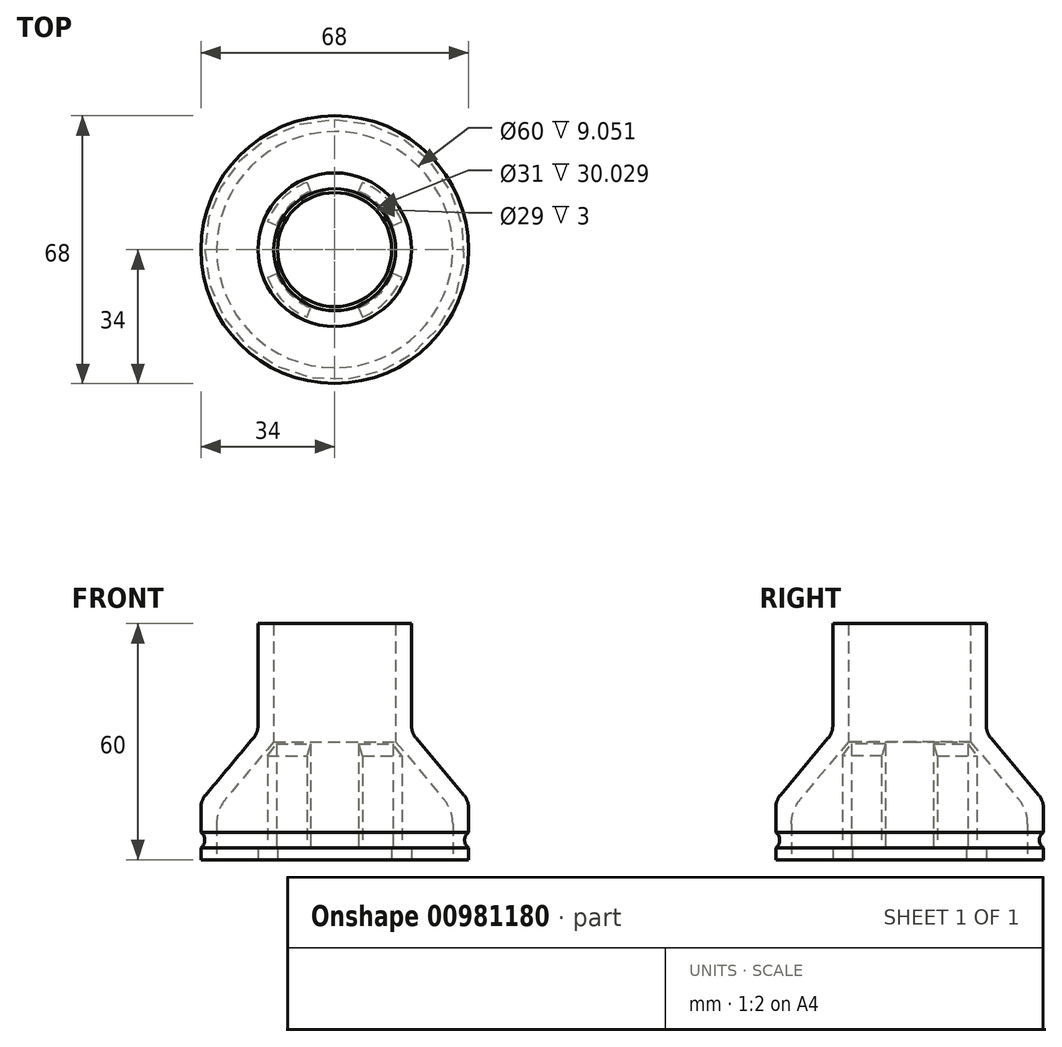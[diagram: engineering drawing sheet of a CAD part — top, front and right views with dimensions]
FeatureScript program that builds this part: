
annotation { "Feature Type Name" : "Feature", "Feature Type Description" : "" }
export const myFeature = defineFeature(function(context is Context, id is Id, definition is map)
    precondition{}
    {
        {
            var Q0;
            Q0=qCreatedBy(makeId("Front.planeOp"),FACE);
            var sketch = newSketch(context, id + "F0", { "sketchPlane" : qUnion([Q0])});
            skLineSegment(sketch, "E0", {"start": v(0, 0) * mm, "end": v(0, 69.55) * mm, "construction": true});
            skLineSegment(sketch, "E1", {"start": v(-30, 0) * mm, "end": v(-30, 12.7) * mm});
            skLineSegment(sketch, "E2", {"start": v(-30, 12.7) * mm, "end": v(-15.5, 29.97) * mm});
            skLineSegment(sketch, "E3", {"start": v(-15.5, 29.97) * mm, "end": v(-15.5, 60) * mm});
            skLineSegment(sketch, "E4", {"start": v(-15.5, 60) * mm, "end": v(-19.5, 60) * mm});
            skLineSegment(sketch, "E5", {"start": v(-19.5, 60) * mm, "end": v(-19.5, 32.28) * mm});
            skLineSegment(sketch, "E6", {"start": v(-19.5, 32.28) * mm, "end": v(-34, 15) * mm});
            skLineSegment(sketch, "E7", {"start": v(-34, 15) * mm, "end": v(-34, 0) * mm});
            skLineSegment(sketch, "E8", {"start": v(-30, 0) * mm, "end": v(-34, 0) * mm});
            skLineSegment(sketch, "E9", {"start": v(-15.5, 29.97) * mm, "end": v(-19.5, 32.28) * mm});
            skLineSegment(sketch, "E10", {"start": v(-30, 12.7) * mm, "end": v(-34, 15) * mm});
            skSolve(sketch);
        }
        {
            var Q0;
            Q0 = qSketchRegion(id + "F0", true);
            var Q1;
            Q1=sQuery(id+"F0.wireOp",EDGE,"E0");
            revolve(context, id + "F1", {"surfaceOperationType" : NewSurfaceOperationType.NEW, "entities" : qUnion([Q0]), "axis" : qUnion([Q1]), "revolveType" : RevolveType.FULL});
        }
        {
            var Q0;
            Q0=makeQuery(id+"F1.opRevolve","SWEPT_FACE",FACE,{"disambiguationData":[OSD([sQuery(id+"F0.wireOp",EDGE,"E8")])]});
            var sketch = newSketch(context, id + "F2", { "sketchPlane" : qUnion([Q0])});
            skCircle(sketch, "E11", {"center": v(0, 0) * mm, "radius": 18.5 * mm});
            skCircle(sketch, "E12", {"center": v(0, 0) * mm, "radius": 16 * mm});
            skLineSegment(sketch, "E13", {"start": v(0, 18.5) * mm, "end": v(0, -18.5) * mm});
            skLineSegment(sketch, "E14", {"start": v(18.5, 0) * mm, "end": v(-18.5, 0) * mm});
            skLineSegment(sketch, "E15", {"start": v(-17.1, -7.08) * mm, "end": v(17.1, 7.08) * mm});
            skLineSegment(sketch, "E16", {"start": v(7.08, 17.1) * mm, "end": v(-7.08, -17.1) * mm});
            skLineSegment(sketch, "E17", {"start": v(17.1, -7.08) * mm, "end": v(-17.1, 7.08) * mm});
            skLineSegment(sketch, "E18", {"start": v(7.08, -17.1) * mm, "end": v(-7.08, 17.1) * mm});
            skSolve(sketch);
        }
        {
            var Q0;
            {var subQ0=sQuery(id+"F2.wireOp",EDGE,"E15");var subQ1=sQuery(id+"F2.wireOp",EDGE,"E11");var subQ2=makeQuery(id+"F2.imprint","INTERSECT",VERTEX,{"disambiguationData":[OD(1.0)],"derivedFrom":[subQ1,subQ0]});Q0=makeQuery(id+"F2.imprint","IMPRINT",FACE,{"disambiguationData":[TD([[makeQuery(id+"F2.imprint","IMPRINT",EDGE,{"disambiguationData":[TD([[subQ2,-1.0]])],"derivedFrom":subQ1}),1.0]])]});}
            var Q1;
            {var subQ0=sQuery(id+"F2.wireOp",EDGE,"E17");var subQ1=sQuery(id+"F2.wireOp",EDGE,"E11");var subQ2=makeQuery(id+"F2.imprint","INTERSECT",VERTEX,{"disambiguationData":[OD(1.0)],"derivedFrom":[subQ1,subQ0]});Q1=makeQuery(id+"F2.imprint","IMPRINT",FACE,{"disambiguationData":[TD([[makeQuery(id+"F2.imprint","IMPRINT",EDGE,{"disambiguationData":[TD([[subQ2,1.0]])],"derivedFrom":subQ1}),1.0]])]});}
            var Q2;
            {var subQ0=sQuery(id+"F2.wireOp",EDGE,"E17");var subQ1=sQuery(id+"F2.wireOp",EDGE,"E11");var subQ2=makeQuery(id+"F2.imprint","INTERSECT",VERTEX,{"disambiguationData":[OD(0.0)],"derivedFrom":[subQ1,subQ0]});Q2=makeQuery(id+"F2.imprint","IMPRINT",FACE,{"disambiguationData":[TD([[makeQuery(id+"F2.imprint","IMPRINT",EDGE,{"disambiguationData":[TD([[subQ2,1.0]])],"derivedFrom":subQ1}),1.0]])]});}
            var Q3;
            {var subQ0=sQuery(id+"F2.wireOp",EDGE,"E15");var subQ1=sQuery(id+"F2.wireOp",EDGE,"E11");var subQ2=makeQuery(id+"F2.imprint","INTERSECT",VERTEX,{"disambiguationData":[OD(0.0)],"derivedFrom":[subQ1,subQ0]});Q3=makeQuery(id+"F2.imprint","IMPRINT",FACE,{"disambiguationData":[TD([[makeQuery(id+"F2.imprint","IMPRINT",EDGE,{"disambiguationData":[TD([[subQ2,-1.0]])],"derivedFrom":subQ1}),1.0]])]});}
            extrude(context, id + "F3", {"entities" : qUnion([Q0, Q1, Q2, Q3]), "operationType" : NewBodyOperationType.ADD, "endBound" : BoundingType.UP_TO_NEXT, "oppositeDirection" : true, "depth" : 25 * mm, "offsetDistance" : 25 * mm});
        }
        {
            var Q0;
            {var subQ0=sQuery(id+"F2.wireOp",EDGE,"E18");var subQ1=sQuery(id+"F2.wireOp",EDGE,"E11");var subQ2=makeQuery(id+"F2.imprint","INTERSECT",VERTEX,{"disambiguationData":[OD(0.0)],"derivedFrom":[subQ1,subQ0]});var subQ3=sQuery(id+"F2.wireOp",EDGE,"E12");var subQ4=makeQuery(id+"F2.imprint","INTERSECT",VERTEX,{"disambiguationData":[OD(1.0)],"derivedFrom":[subQ3,subQ0]});var subQ5=sQuery(id+"F2.wireOp",EDGE,"E17");var subQ6=makeQuery(id+"F2.imprint","INTERSECT",VERTEX,{"disambiguationData":[OD(0.0)],"derivedFrom":[subQ1,subQ5]});Q0=makeQuery(id+"F3.opExtrude","CAP_FACE",FACE,{"disambiguationData":[OSD([subQ1,subQ3,subQ5,subQ0]),TDD([makeQuery(id+"F2.imprint","IMPRINT",EDGE,{"disambiguationData":[TD([[subQ6,1.0]])],"derivedFrom":subQ1}),makeQuery(id+"F2.imprint","IMPRINT",EDGE,{"disambiguationData":[TD([[subQ4,-1.0]])],"derivedFrom":subQ3}),makeQuery(id+"F2.imprint","IMPRINT",EDGE,{"disambiguationData":[TD([[subQ6,-1.0]])],"derivedFrom":subQ5}),makeQuery(id+"F2.imprint","IMPRINT",EDGE,{"disambiguationData":[TD([[subQ2,-1.0]])],"derivedFrom":subQ0})])],"isStart":true});}
            var sketch = newSketch(context, id + "F4", { "sketchPlane" : qUnion([Q0])});
            skCircle(sketch, "E19", {"center": v(0, 0) * mm, "radius": 14.5 * mm});
            skCircle(sketch, "E20", {"center": v(0, 0) * mm, "radius": 19.5 * mm});
            skSolve(sketch);
        }
        {
            var Q0;
            Q0 = qSketchRegion(id + "F4", true);
            extrude(context, id + "F5", {"entities" : qUnion([Q0]), "operationType" : NewBodyOperationType.ADD, "oppositeDirection" : true, "depth" : 3 * mm, "offsetDistance" : 25 * mm});
        }
        {
            var Q0;
            Q0=qCreatedBy(makeId("Front.planeOp"),FACE);
            var sketch = newSketch(context, id + "F6", { "sketchPlane" : qUnion([Q0])});
            skCircle(sketch, "E21", {"center": v(35.5, 5) * mm, "radius": 2.5 * mm});
            skLineSegment(sketch, "E22", {"start": v(0, -8.3) * mm, "end": v(0, 11.78) * mm, "construction": true});
            skSolve(sketch);
        }
        {
            var Q0;
            Q0 = qSketchRegion(id + "F6", true);
            var Q1;
            Q1=sQuery(id+"F6.wireOp",EDGE,"E22");
            revolve(context, id + "F7", {"operationType" : NewBodyOperationType.REMOVE, "surfaceOperationType" : NewSurfaceOperationType.NEW, "entities" : qUnion([Q0]), "axis" : qUnion([Q1]), "revolveType" : RevolveType.FULL, "oppositeDirection" : true});
        }
        {
            var Q0;
            Q0=makeQuery(id+"F1.opRevolve","SWEPT_EDGE",EDGE,{"disambiguationData":[OSD([sQuery(id+"F0.wireOp",EDGE,"E1"),sQuery(id+"F0.wireOp",EDGE,"E2"),sQuery(id+"F0.wireOp",EDGE,"E10")])]});
            fillet(context, id + "F8", {"entities" : qUnion([Q0]), "radius" : 10 * mm, "tangentPropagation" : true, "allowEdgeOverflow" : false});
        }
        {
            var Q0;
            Q0=makeQuery(id+"F1.opRevolve","SWEPT_EDGE",EDGE,{"disambiguationData":[OSD([sQuery(id+"F0.wireOp",EDGE,"E6"),sQuery(id+"F0.wireOp",EDGE,"E7"),sQuery(id+"F0.wireOp",EDGE,"E10")])]});
            fillet(context, id + "F9", {"entities" : qUnion([Q0]), "radius" : 5 * mm, "tangentPropagation" : true, "allowEdgeOverflow" : false});
        }
        {
            var Q0;
            Q0=makeQuery(id+"F1.opRevolve","SWEPT_EDGE",EDGE,{"disambiguationData":[OSD([sQuery(id+"F0.wireOp",EDGE,"E5"),sQuery(id+"F0.wireOp",EDGE,"E6"),sQuery(id+"F0.wireOp",EDGE,"E9")])]});
            fillet(context, id + "F10", {"entities" : qUnion([Q0]), "radius" : 5 * mm, "tangentPropagation" : true, "allowEdgeOverflow" : false});
        }
    });
